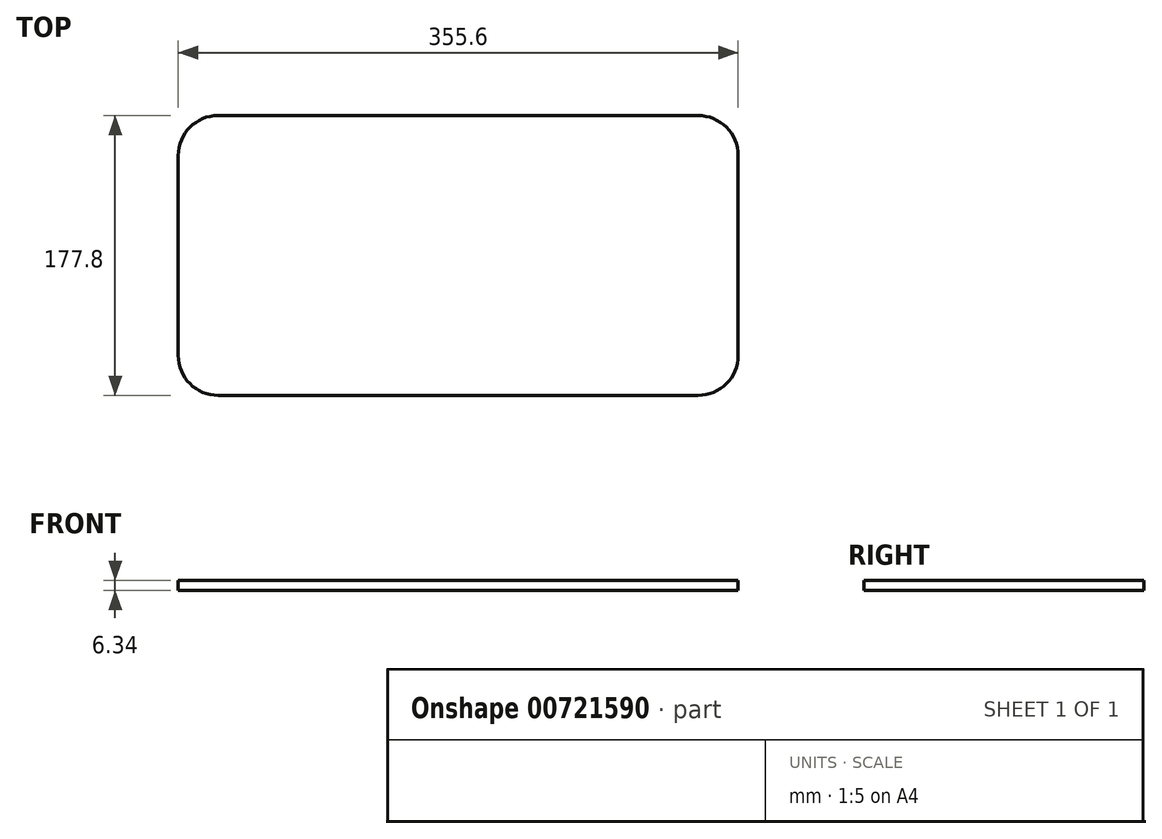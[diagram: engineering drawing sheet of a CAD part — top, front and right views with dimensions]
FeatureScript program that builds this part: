
annotation { "Feature Type Name" : "Feature", "Feature Type Description" : "" }
export const myFeature = defineFeature(function(context is Context, id is Id, definition is map)
    precondition{}
    {
        {
            var Q0;
            Q0=qCreatedBy(makeId("Top.planeOp"),FACE);
            var sketch = newSketch(context, id + "F0", { "sketchPlane" : qUnion([Q0])});
            skLineSegment(sketch, "E0.bottom", {"start": v(152.4, -62.94) * mm, "end": v(-152.4, -62.94) * mm});
            skLineSegment(sketch, "E0.top", {"start": v(152.4, 62.94) * mm, "end": v(-152.4, 62.94) * mm});
            skLineSegment(sketch, "E0.left", {"start": v(152.4, -62.94) * mm, "end": v(152.4, 62.94) * mm});
            skLineSegment(sketch, "E0.right", {"start": v(-152.4, -62.94) * mm, "end": v(-152.4, 62.94) * mm});
            skPoint(sketch, "E0.middle", {"position": v(0, 0) * mm});
            skSolve(sketch);
        }
        {
            var Q0;
            Q0=makeQuery(id+"F0.imprint","IMPRINT",FACE,{"disambiguationData":[TD([[makeQuery(id+"F0.imprint","IMPRINT",EDGE,{"derivedFrom":sQuery(id+"F0.wireOp",EDGE,"E0.bottom")}),-1.0]])]});
            extrude(context, id + "F1", {"entities" : qUnion([Q0]), "depth" : 6.35 * mm, "offsetDistance" : 25.4 * mm, "symmetric" : true});
        }
        {
            var Q0;
            Q0=qCreatedBy(makeId("Top.planeOp"),FACE);
            var sketch = newSketch(context, id + "F2", { "sketchPlane" : qUnion([Q0])});
            skLineSegment(sketch, "E1.bottom", {"start": v(177.8, -88.9) * mm, "end": v(-177.8, -88.9) * mm});
            skLineSegment(sketch, "E1.top", {"start": v(177.8, 88.9) * mm, "end": v(-177.8, 88.9) * mm});
            skLineSegment(sketch, "E1.left", {"start": v(177.8, -88.9) * mm, "end": v(177.8, 88.9) * mm});
            skLineSegment(sketch, "E1.right", {"start": v(-177.8, -88.9) * mm, "end": v(-177.8, 88.9) * mm});
            skPoint(sketch, "E1.middle", {"position": v(0, 0) * mm});
            skSolve(sketch);
        }
        {
            var Q0;
            Q0=qSketchRegion(id+"F2",true);
            extrude(context, id + "F3", {"entities" : qUnion([Q0]), "operationType" : NewBodyOperationType.ADD, "depth" : 6.35 * mm, "offsetDistance" : 25.4 * mm, "symmetric" : true});
        }
        {
            var Q0;
            Q0=makeQuery(id+"F3.opExtrude","SWEPT_EDGE",EDGE,{"disambiguationData":[OSD([sQuery(id+"F2.wireOp",EDGE,"E1.top"),sQuery(id+"F2.wireOp",EDGE,"E1.right")])]});
            fillet(context, id + "F4", {"entities" : qUnion([Q0]), "radius" : 25.4 * mm, "tangentPropagation" : true, "allowEdgeOverflow" : false});
        }
        {
            var Q0;
            Q0=makeQuery(id+"F3.opExtrude","SWEPT_EDGE",EDGE,{"disambiguationData":[OSD([sQuery(id+"F2.wireOp",EDGE,"E1.top"),sQuery(id+"F2.wireOp",EDGE,"E1.left")])]});
            fillet(context, id + "F5", {"entities" : qUnion([Q0]), "radius" : 25.4 * mm, "tangentPropagation" : true, "allowEdgeOverflow" : false});
        }
        {
            var Q0;
            Q0=makeQuery(id+"F3.opExtrude","SWEPT_EDGE",EDGE,{"disambiguationData":[OSD([sQuery(id+"F2.wireOp",EDGE,"E1.bottom"),sQuery(id+"F2.wireOp",EDGE,"E1.left")])]});
            fillet(context, id + "F6", {"entities" : qUnion([Q0]), "radius" : 25.4 * mm, "tangentPropagation" : true, "allowEdgeOverflow" : false});
        }
        {
            var Q0;
            Q0=makeQuery(id+"F3.opExtrude","SWEPT_EDGE",EDGE,{"disambiguationData":[OSD([sQuery(id+"F2.wireOp",EDGE,"E1.bottom"),sQuery(id+"F2.wireOp",EDGE,"E1.right")])]});
            fillet(context, id + "F7", {"entities" : qUnion([Q0]), "radius" : 25.4 * mm, "tangentPropagation" : true, "allowEdgeOverflow" : false});
        }
    });
